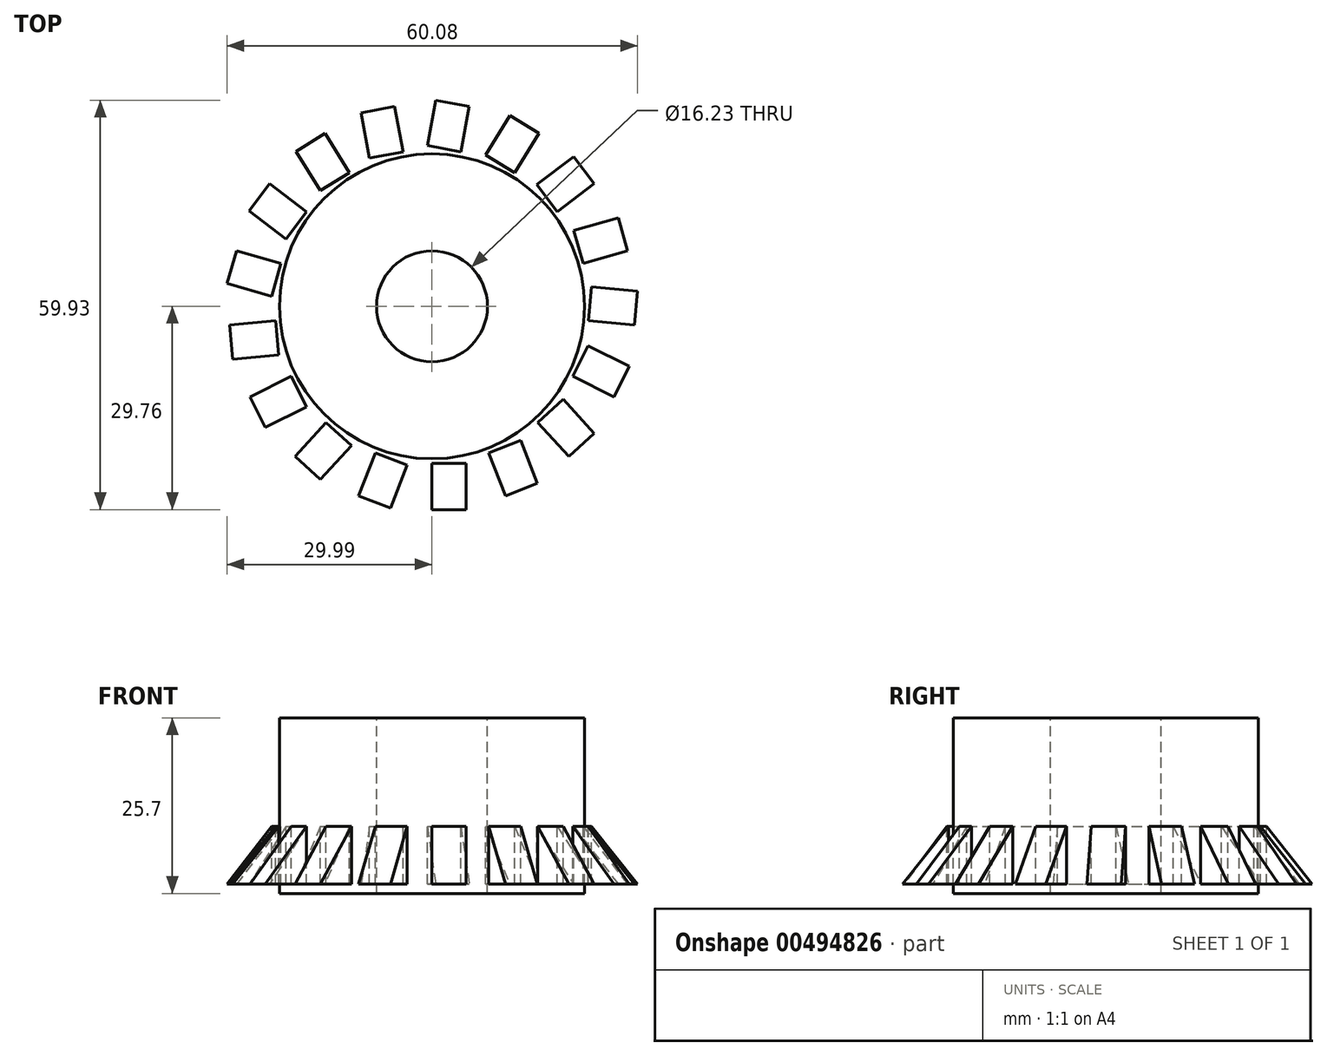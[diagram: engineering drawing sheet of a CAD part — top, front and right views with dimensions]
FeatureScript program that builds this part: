
annotation { "Feature Type Name" : "Feature", "Feature Type Description" : "" }
export const myFeature = defineFeature(function(context is Context, id is Id, definition is map)
    precondition{}
    {
        {
            var Q0;
            Q0=qCreatedBy(makeId("Front.planeOp"),FACE);
            var sketch = newSketch(context, id + "F0", { "sketchPlane" : qUnion([Q0])});
            skLineSegment(sketch, "E0", {"start": v(0, 37.03) * mm, "end": v(0, -41.09) * mm});
            skLineSegment(sketch, "E1", {"start": v(-8.12, 11.67) * mm, "end": v(-8.12, -14.03) * mm});
            skLineSegment(sketch, "E2", {"start": v(-8.12, -14.03) * mm, "end": v(-22.32, -14.03) * mm});
            skLineSegment(sketch, "E3", {"start": v(-22.32, -14.03) * mm, "end": v(-22.32, 11.67) * mm});
            skLineSegment(sketch, "E4", {"start": v(-22.32, 11.67) * mm, "end": v(-8.12, 11.67) * mm});
            skSolve(sketch);
        }
        {
            var Q0;
            Q0=makeQuery(id+"F0.imprint","IMPRINT",FACE,{"disambiguationData":[TD([[makeQuery(id+"F0.imprint","IMPRINT",EDGE,{"derivedFrom":sQuery(id+"F0.wireOp",EDGE,"E1")}),-1.0]])]});
            var Q1;
            Q1=sQuery(id+"F0.wireOp",EDGE,"E0");
            revolve(context, id + "F1", {"entities" : qUnion([Q0]), "axis" : qUnion([Q1]), "revolveType" : RevolveType.FULL});
        }
        {
            var Q0;
            Q0=qCreatedBy(makeId("Right.planeOp"),FACE);
            var sketch = newSketch(context, id + "F2", { "sketchPlane" : qUnion([Q0])});
            skLineSegment(sketch, "E5", {"start": v(-23, -4.23) * mm, "end": v(-29.76, -12.68) * mm});
            skLineSegment(sketch, "E6", {"start": v(-29.76, -12.68) * mm, "end": v(-23, -12.68) * mm});
            skLineSegment(sketch, "E7", {"start": v(-23, -12.68) * mm, "end": v(-23, -4.23) * mm});
            skSolve(sketch);
        }
        {
            var Q0;
            Q0=makeQuery(id+"F2.imprint","IMPRINT",FACE,{"disambiguationData":[TD([[makeQuery(id+"F2.imprint","IMPRINT",EDGE,{"derivedFrom":sQuery(id+"F2.wireOp",EDGE,"E5")}),1.0]])]});
            extrude(context, id + "F3", {"entities" : qUnion([Q0]), "depth" : 5 * mm});
        }
        {
            var Q0;
            Q0=makeQuery(id+"F3.opExtrude","SWEPT_BODY",BODY,{"disambiguationData":[OSD([sQuery(id+"F2.wireOp",EDGE,"E5"),sQuery(id+"F2.wireOp",EDGE,"E6"),sQuery(id+"F2.wireOp",EDGE,"E7")])]});
            var Q1;
            Q1=sQuery(id+"F0.wireOp",EDGE,"E0");
            circularPattern(context, id + "F4", {"entities" : qUnion([Q0]), "axis" : qUnion([Q1]), "angle" : 360 * degree, "instanceCount" : 17, "equalSpace" : true});
        }
    });
